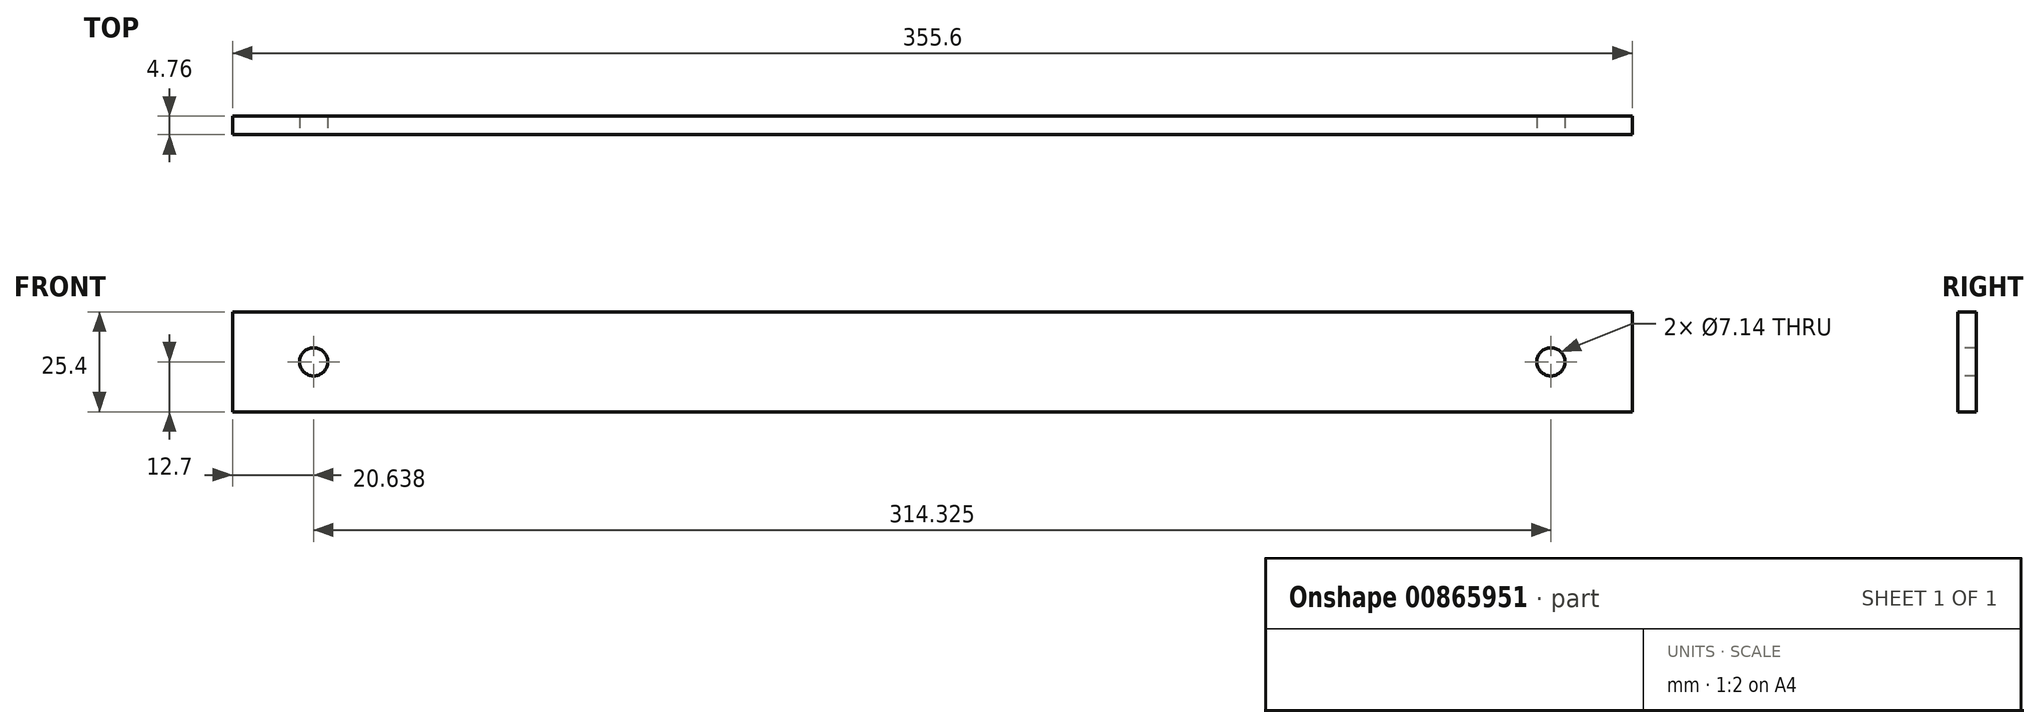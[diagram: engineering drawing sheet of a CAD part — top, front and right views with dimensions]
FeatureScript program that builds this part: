
annotation { "Feature Type Name" : "Feature", "Feature Type Description" : "" }
export const myFeature = defineFeature(function(context is Context, id is Id, definition is map)
    precondition{}
    {
        {
            var Q0;
            Q0=qCreatedBy(makeId("Front.planeOp"),FACE);
            var sketch = newSketch(context, id + "F0", { "sketchPlane" : qUnion([Q0])});
            skLineSegment(sketch, "E0.bottom", {"start": v(-177.8, 12.7) * mm, "end": v(177.8, 12.7) * mm});
            skLineSegment(sketch, "E0.top", {"start": v(-177.8, -12.7) * mm, "end": v(177.8, -12.7) * mm});
            skLineSegment(sketch, "E0.left", {"start": v(-177.8, 12.7) * mm, "end": v(-177.8, -12.7) * mm});
            skLineSegment(sketch, "E0.right", {"start": v(177.8, 12.7) * mm, "end": v(177.8, -12.7) * mm});
            skLineSegment(sketch, "E1", {"start": v(-177.8, 12.7) * mm, "end": v(177.8, -12.7) * mm, "construction": true});
            skLineSegment(sketch, "E2", {"start": v(-177.8, -12.7) * mm, "end": v(177.8, 12.7) * mm, "construction": true});
            skPoint(sketch, "E3", {"position": v(-157.16, 0) * mm});
            skPoint(sketch, "E4", {"position": v(157.16, 0) * mm});
            skSolve(sketch);
        }
        {
            var Q0;
            Q0 = qSketchRegion(id + "F0", true);
            extrude(context, id + "F1", {"entities" : qUnion([Q0]), "depth" : 4.76 * mm, "offsetDistance" : 25.4 * mm});
        }
        {
            var Q0;
            Q0=sQuery(id+"F0.wireOp",VERTEX,"E3");
            var Q1;
            Q1=sQuery(id+"F0.wireOp",VERTEX,"E4");
            var Q2;
            Q2=makeQuery(id+"F1.opExtrude","SWEPT_BODY",BODY,{"disambiguationData":[OSD([sQuery(id+"F0.wireOp",EDGE,"E0.bottom"),sQuery(id+"F0.wireOp",EDGE,"E0.top"),sQuery(id+"F0.wireOp",EDGE,"E0.left"),sQuery(id+"F0.wireOp",EDGE,"E0.right")])]});
            hole(context, id + "F2", {"style" : HoleStyle.SIMPLE, "endStyle" : HoleEndStyle.THROUGH, "oppositeDirection" : true, "standardTappedOrClearance" : lookupTablePath({ "fit" : "Normal (ASME)", "standard" : "ANSI", "size" : "1/4", "type" : "Clearance" }), "standardBlindInLast" : lookupTablePath({ "fit" : "Normal", "standard" : "ANSI", "engagement" : "75%", "pitch" : "20 tpi", "size" : "1/4", "type" : "Clearance & tapped" }), "holeDiameter" : 7.14 * mm, "majorDiameter" : 3.5 * mm, "isTappedThrough" : true, "tappedDepth" : 16.67 * mm, "tapClearance" : 3, "locations" : qUnion([Q0, Q1]), "scope" : qUnion([Q2]), "startStyle" : HoleStartStyle.PART});
        }
    });
